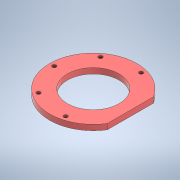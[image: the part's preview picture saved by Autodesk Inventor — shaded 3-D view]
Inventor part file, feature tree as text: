
AUTODESK INVENTOR PART (.ipt)
format: ipt  version: 2022 (Build 260153000, 153)  size: 129,536 bytes
history: native  units: mm
features: extrude x1, sketch x1
ambient origin geometry x8: Origin, YZ Plane, XZ Plane, XY Plane, X Axis, Y Axis, Z Axis, Center Point
bodies: Body1 (feature_tree)
feature tree (2):
  extrude  "Выдавливание3"  Depth=28.0mm
  sketch  "Эскиз1"
